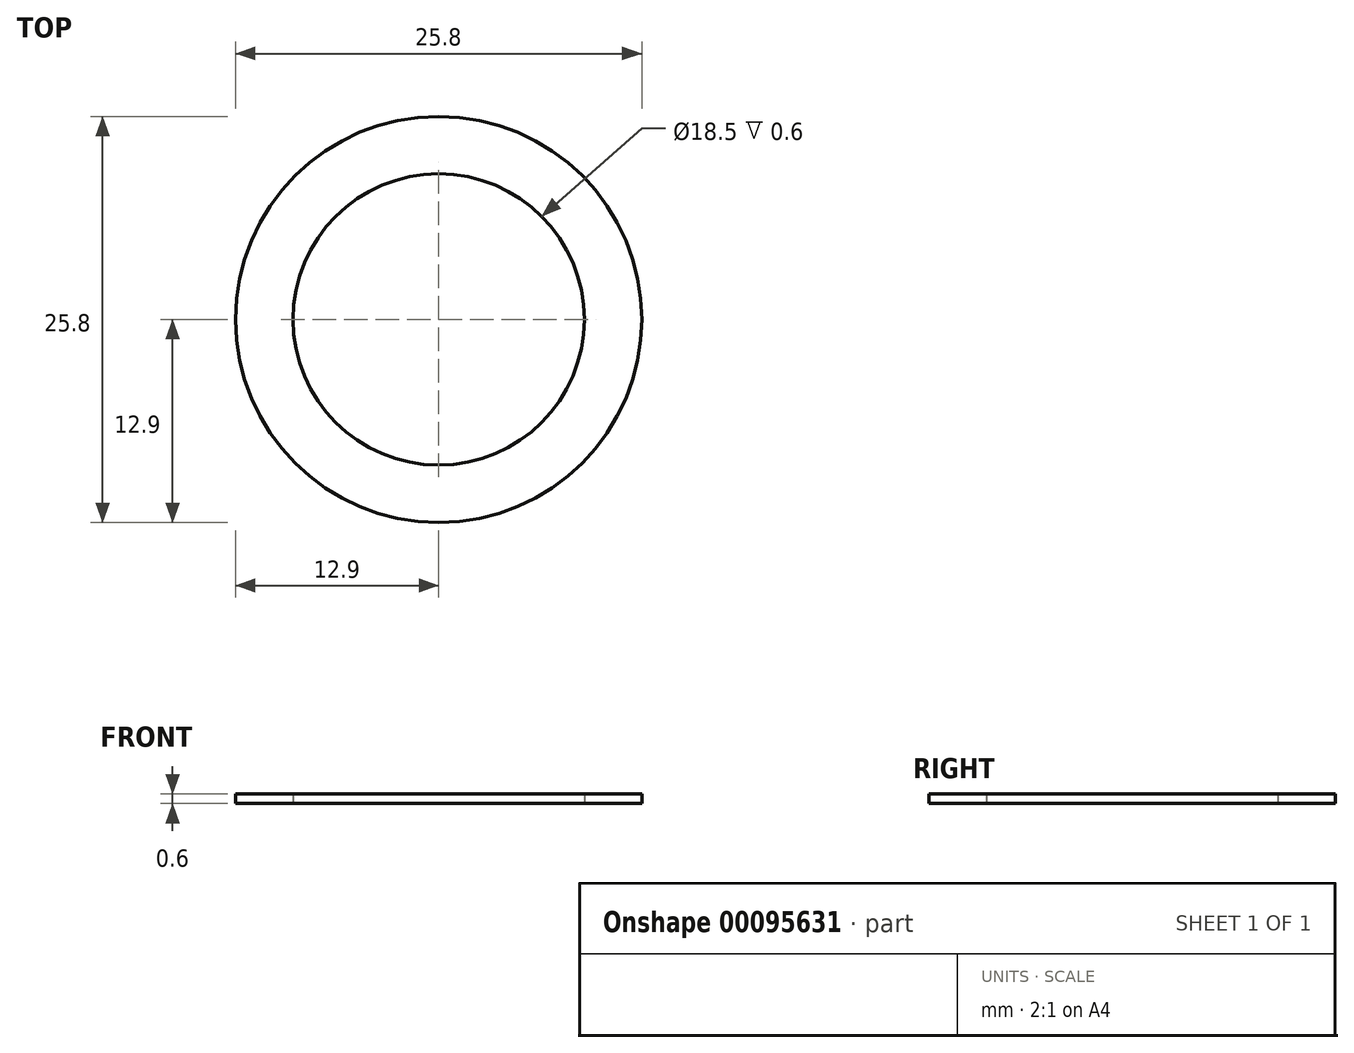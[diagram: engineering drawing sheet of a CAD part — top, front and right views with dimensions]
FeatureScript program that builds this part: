
annotation { "Feature Type Name" : "Feature", "Feature Type Description" : "" }
export const myFeature = defineFeature(function(context is Context, id is Id, definition is map)
    precondition{}
    {
        {
            var Q0;
            Q0=qCreatedBy(makeId("Top.planeOp"),FACE);
            var sketch = newSketch(context, id + "F0", { "sketchPlane" : qUnion([Q0])});
            skCircle(sketch, "E0", {"center": v(0, 0) * mm, "radius": 12.9 * mm});
            skCircle(sketch, "E1", {"center": v(0, 0) * mm, "radius": 9.25 * mm});
            skSolve(sketch);
        }
        {
            var Q0;
            Q0=qSketchRegion(id+"F0",true);
            extrude(context, id + "F1", {"entities" : qUnion([Q0]), "depth" : .6 * mm});
        }
    });
